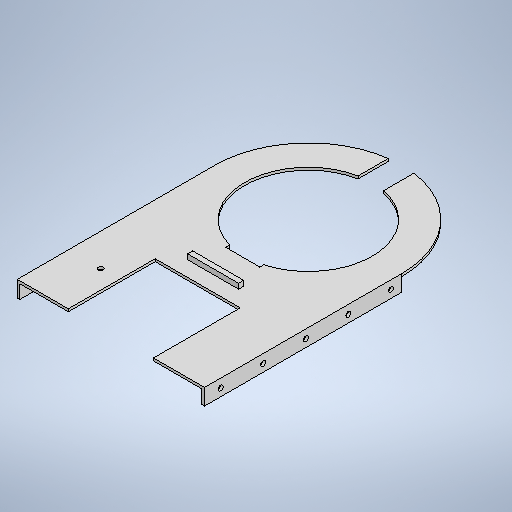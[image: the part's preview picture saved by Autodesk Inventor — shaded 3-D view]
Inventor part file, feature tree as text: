
AUTODESK INVENTOR PART (.ipt)
format: ipt  version: 2025 (Build 290162010, 162A)  size: 335,872 bytes
history: native  units: mm
features: sketch x7, extrude x6, hole x2, mirror x1, projected_geometry x1
ambient origin geometry x8: Origin, YZ Plane, XZ Plane, XY Plane, X Axis, Y Axis, Z Axis, Center Point
bodies: Volumenkörper1 (feature_tree)
feature tree (17):
  extrude  "Extrusion1"  Depth=51.0mm
  extrude  "Extrusion2"  Depth=55.0mm
  sketch  "Skizze3"  dims[d4=1.5mm d5=0.0mm d6=75.0mm]
  extrude  "Extrusion3"  Depth=1.5mm
  extrude  "Extrusion4"  Depth=15.0mm
  extrude  "Extrusion5"  Depth=20.0mm
  extrude  "Extrusion7"  Depth=10.0mm TaperAngle=0.0deg
  hole  "Hole1"  [1 undecoded]
  mirror  "Mirror1"
  hole  "Hole2"  [1 undecoded]
  sketch  "Skizze1"  dims[d0=25.0mm d1=51.0mm]
  sketch  "Skizze2"  dims[d2=116.0mm d3=55.0mm]
  projected_geometry  "Projizierte Kontur1"
  sketch  "Skizze5"  dims[d7=1.5mm d8=0.0mm d9=15.0mm]
  sketch  "Sketch8"  dims[d10=10.0mm d11=0.0mm d12=20.0mm]
  sketch  "Sketch9"  dims[d13=1.0mm d14=10.0mm d15=0.0mm]
  sketch  "Sketch10"  dims[d16=3.0mm d17=30.0mm d18=60.0mm d19=3.0mm d20=0.0mm d26=25.0mm d27=25.0mm d28=25.0mm d29=25.0mm d30=5.0mm d31=3.0mm d32=6.0mm d33=4.0mm d34=2.0mm d35=90.0deg d36=8.0mm d37=0.0mm d39=8.0mm d40=1.5mm d41=0.0mm d42=30.0mm d43=19.0mm d44=3.0mm d45=6.0mm d46=4.0mm d47=2.0mm d48=90.0deg d49=8.0mm d50=0.0mm]
note: 2 required parameter values undecoded (feature->parameter linkage not recoverable at this tier; creation-order binding heuristic only, values carry confidence <= 0.55)
